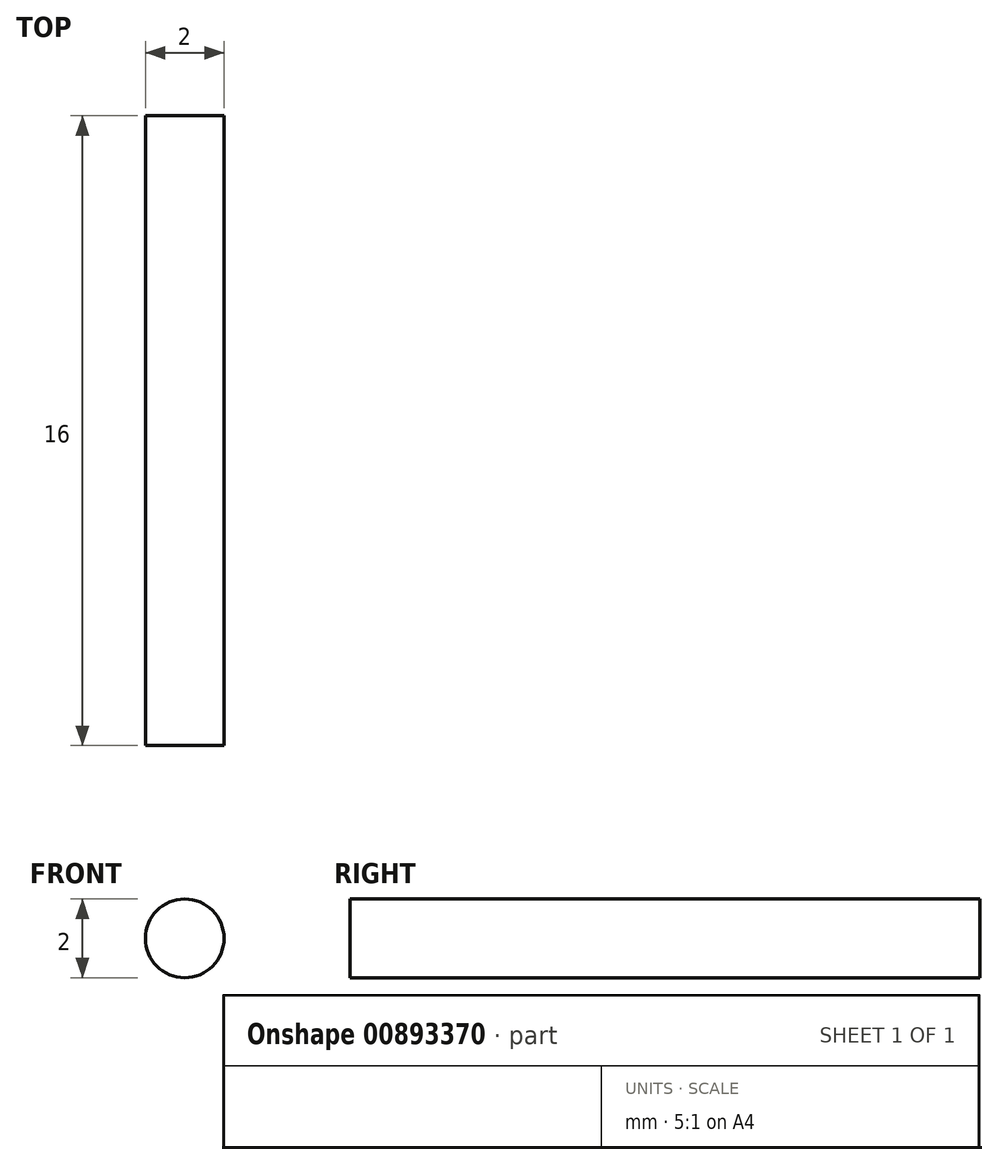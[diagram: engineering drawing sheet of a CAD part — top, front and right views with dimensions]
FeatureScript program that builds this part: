
annotation { "Feature Type Name" : "Feature", "Feature Type Description" : "" }
export const myFeature = defineFeature(function(context is Context, id is Id, definition is map)
    precondition{}
    {
        {
            var Q0;
            Q0=qCreatedBy(makeId("Front.planeOp"),FACE);
            var sketch = newSketch(context, id + "F0", { "sketchPlane" : qUnion([Q0])});
            skCircle(sketch, "E0", {"center": v(0, 0) * mm, "radius": 1 * mm});
            skSolve(sketch);
        }
        {
            var Q0;
            Q0 = qSketchRegion(id + "F0", true);
            extrude(context, id + "F1", {"entities" : qUnion([Q0]), "depth" : 16 * mm, "offsetDistance" : 25 * mm});
        }
    });
